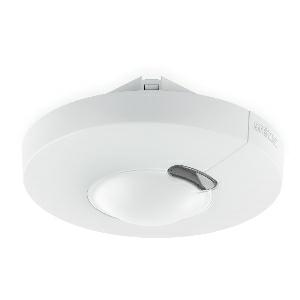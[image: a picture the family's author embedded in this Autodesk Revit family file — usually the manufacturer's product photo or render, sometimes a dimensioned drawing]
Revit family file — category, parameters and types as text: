
# Revit family: hf_3360_057343
name_source: partatom
category: Elektroinstallationen
revit_build: Autodesk Revit 2016 (Build: 20190508_0715(x64)
units: mm (PartAtom-declared; Revit-internal decimal feet)

## family parameters
Basisbauteil = Fläche
Beim Laden mit Abzugskörper schneiden = Nein
Bemaßung runder Anschluss = Durchmesser verwenden
Beschriftungsausrichtung beibehalten = Nein
Gemeinsam genutzt = Nein
Raumberechnungspunkt = Nein
Teiletyp = Normal

## types (1)
- HF 3360
    Apparent Load = 0 VA
    Beschreibung = Type: Motion detectors; Dimensions (Ø x H): 124 x 95 mm; Mains power supply: 12 – 22,5 V; Power consumption: 0,5 W; Sensor Technology: High frequency; Application, place: Indoors; Application, room: function room / ancillary room, stairwell, WC / washroom, multi-storey / underground car park, Indoors; Installation site: wall, ceiling, corner; Installation: Concealed wiring; HF-system: 5,8 GHz; Electronic scalability: Yes; Mechanical scalability: No; Mounting height: 2,00 – 4,00 m; Optimum mounting height: 2,8 m; Detection: also through glass, wood and stud walls; Detection angle: 360 °; Angle of aperture: 160 °; Sneak-by guard: Yes; Reach, radial: Ø 8 m (50 m²); Reach, tangential: Ø 8 m (50 m²); Twilight setting TEACH: No; Twilight setting: 2 – 1000 lx; Control output, Dali: Addressable/slave; Constant-lighting control: No; Basic light level function: No; With bus coupling: Yes; Settings via: Bus; With remote control: No; IP-rating: IP20; Material: Plastic; Ambient temperature: -20 – 50 °C; Colour: white; Colour, RAL: 9003; Manufacturer's Warranty: 5 years; Version: DALI-2 IPD - concealed, rd.; PU1, EAN: 4007841057343
    Height = 0 mm  [stored 0 ft]
    Hersteller = Steinel
    Length = 124 mm  [stored 0.406824 ft]
    ModVariant = Nein
    Modell = 057343
    Mounting Type = Recessed
    Number of Poles = 1
    OnlyDefault = Ja
    Power Factor = 1
    Product Name = HF 3360
    Product group = Sensor-switched indoor light
    ProductGroupID = 30
    Protection Class = Protection class
    Protection Degree = IP 20
    RlxData = <blob elided: 36133 chars, md5=a0fb63d1>
    SensorDataFile = {"IESDataFiles":[]}
    Typenbild = produkt1_057343.jpg
    Typenkommentare = Product without accessories
    URL = http://relux.com
    VarID = ---
    Voltage = 0 V
    Vorgabe-Ansicht = 1800 mm
    Weight = 0.00 kg
    Width = 0 mm  [stored 0 ft]

note: [stored X ft] marks values corroborated as IEEE doubles in the binary element streams (Revit-internal decimal feet)

## geometry (parser evidence)
native form markers: Sweep x12
no freeform markers — native parametric forms only
